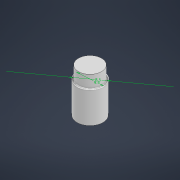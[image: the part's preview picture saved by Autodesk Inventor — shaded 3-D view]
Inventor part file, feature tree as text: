
AUTODESK INVENTOR PART (.ipt)
format: ipt  version: 2022 (Build 260153000, 153)  size: 94,720 bytes
history: native  units: mm
features: extrude x2, sketch x1
ambient origin geometry x8: Origin, YZ Plane, XZ Plane, XY Plane, X Axis, Y Axis, Z Axis, Center Point
bodies: Solid1 (feature_tree)
feature tree (3):
  sketch  "Sketch1"  dims[d0=8.5mm d1=9.5mm d2=4.5mm d3=0.0mm d4=11.5mm d5=0.0mm]
  extrude  "Extrusion1"  Depth=11.5mm
  extrude  "Extrusion2"  Depth=4.5mm TaperAngle=0.0deg
